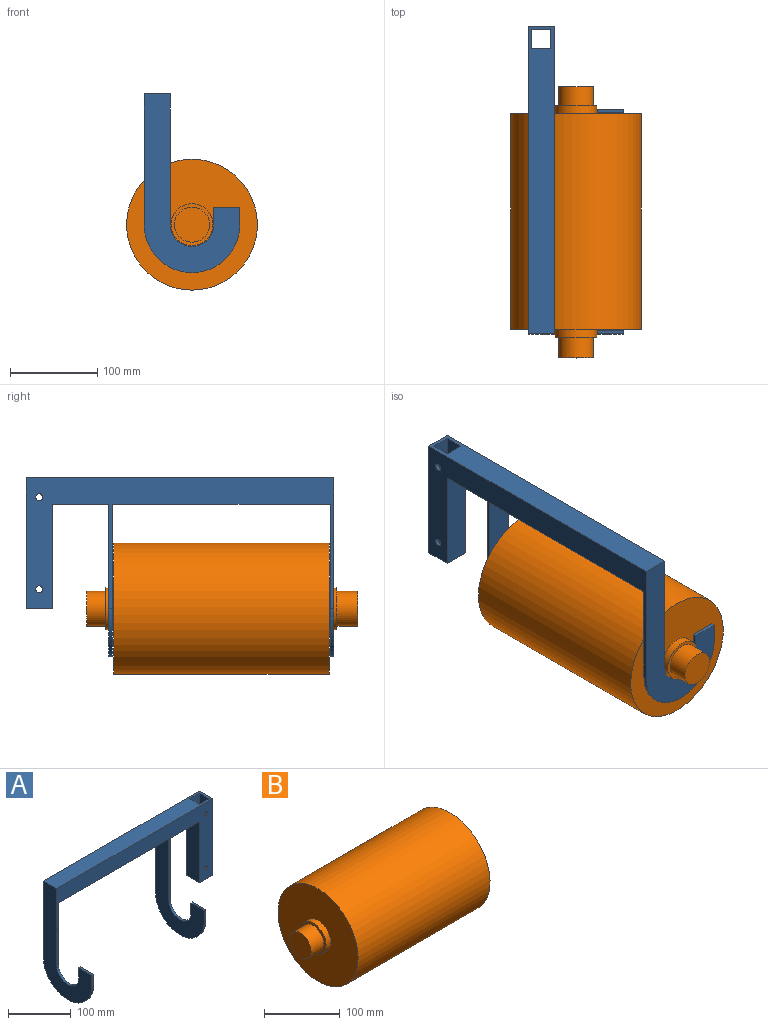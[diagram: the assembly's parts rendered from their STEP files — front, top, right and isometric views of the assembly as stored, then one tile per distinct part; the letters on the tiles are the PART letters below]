
ASSEMBLY  parts=2 mates=1
PART A: 42 faces, bbox 353x110x205 mm
  f0: plane 175x110mm, normal (1,0,0), area 7969.9mm2, adj f1,f7,f13,f14,f15,f16,f17,f27
  f1: plane 353x150mm, normal (0,-1,0), area 15049.5mm2, adj f0,f2,f8,f9,f10,f11,f12,f17
  f2: cylinder r=25mm len=50mm, axis (1,0,0), area 314.2mm2, adj f1,f3,f9,f10
  f3: plane 20x4mm, normal (0,1,0), area 80mm2, adj f2,f4,f9,f10
  f4: plane 30x4mm, normal (0,0,1), area 120mm2, adj f3,f5,f9,f10
  f5: plane 20x4mm, normal (0,-1,0), area 80mm2, adj f4,f6,f9,f10
  f6: cylinder r=55mm len=110mm, axis (1,0,0), area 691.2mm2, adj f5,f7,f9,f10
  f7: plane 353x150mm, normal (0,1,0), area 15049.5mm2, adj f0,f6,f8,f9,f10,f11,f12,f13
  f8: plane 353x30mm, normal (0,0,1), area 10106mm2, adj f1,f7,f9,f22,f24,f25,f28,f29
  f9: plane 205x110mm, normal (-1,0,0), area 8869.9mm2, adj f1,f2,f3,f4,f5,f6,f7,f8
  f10: plane 175x110mm, normal (1,0,0), area 7969.9mm2, adj f1,f2,f3,f4,f5,f6,f7,f11
  f11: plane 250x30mm, normal (0,0,-1), area 7500mm2, adj f1,f7,f10,f12
  f12: plane 175x110mm, normal (-1,0,0), area 7969.9mm2, adj f1,f7,f11,f13,f14,f15,f16,f17
  f13: cylinder r=55mm len=110mm, axis (-1,0,0), area 691.2mm2, adj f0,f7,f12,f14
  f14: plane 20x4mm, normal (0,-1,0), area 80mm2, adj f0,f12,f13,f15
  f15: plane 30x4mm, normal (0,0,1), area 120mm2, adj f0,f12,f14,f16
  f16: plane 20x4mm, normal (0,1,0), area 80mm2, adj f0,f12,f15,f17
  f17: cylinder r=25mm len=50mm, axis (-1,0,0), area 314.2mm2, adj f0,f1,f12,f16
  f18: cylinder r=4mm len=8mm, axis (0,-1,0), area 100.5mm2, adj f7,f29
  f19: cylinder r=4mm len=8mm, axis (0,-1,0), area 100.5mm2, adj f7,f29
  f20: cylinder r=4mm len=8mm, axis (0,-1,0), area 100.5mm2, adj f1,f28
  f21: cylinder r=4mm len=8mm, axis (0,-1,0), area 100.5mm2, adj f1,f28
  f22: plane 150x22mm, normal (1,0,0), area 3300mm2, adj f8,f26,f28,f29
  f23: plane 120x30mm, normal (-1,0,0), area 3600mm2, adj f1,f7,f26,f27
  f24: plane 150x30mm, normal (1,0,0), area 4500mm2, adj f1,f7,f8,f26
  f25: plane 150x22mm, normal (-1,0,0), area 3300mm2, adj f8,f26,f28,f29
  f26: plane 30x30mm, normal (0,0,-1), area 416mm2, adj f1,f7,f22,f23,f24,f25,f28,f29
  f27: plane 65x30mm, normal (0,0,-1), area 1950mm2, adj f0,f1,f7,f23
  f28: plane 150x22mm, normal (0,1,0), area 3199.5mm2, adj f8,f20,f21,f22,f25,f26
  f29: plane 150x22mm, normal (0,-1,0), area 3199.5mm2, adj f8,f18,f19,f22,f25,f26
  f30: plane 22x22mm, normal (1,0,0), area 484mm2, adj f31,f32,f33,f34
  f31: plane 250x22mm, normal (0,-1,0), area 5500mm2, adj f30,f32,f34,f35
  f32: plane 250x22mm, normal (0,0,-1), area 5500mm2, adj f30,f31,f33,f35
  f33: plane 250x22mm, normal (0,1,0), area 5500mm2, adj f30,f32,f34,f35
  f34: plane 250x22mm, normal (0,0,1), area 5500mm2, adj f30,f31,f33,f35
  f35: plane 22x22mm, normal (-1,0,0), area 484mm2, adj f31,f32,f33,f34
  f36: plane 65x22mm, normal (0,0,-1), area 1430mm2, adj f37,f39,f40,f41
  f37: plane 65x22mm, normal (0,-1,0), area 1430mm2, adj f36,f38,f40,f41
  f38: plane 65x22mm, normal (0,0,1), area 1430mm2, adj f37,f39,f40,f41
  f39: plane 65x22mm, normal (0,1,0), area 1430mm2, adj f36,f38,f40,f41
  f40: plane 22x22mm, normal (-1,0,0), area 484mm2, adj f36,f37,f38,f39
  f41: plane 22x22mm, normal (1,0,0), area 484mm2, adj f36,f37,f38,f39
PART B: 11 faces, bbox 311x150x150 mm
  f0: cylinder r=75mm len=247mm, axis (-1,0,0), area 116396mm2, adj f1,f2
  f1: plane 150x150mm, normal (1,0,0), area 15861.9mm2, adj f0,f3
  f2: plane 150x150mm, normal (-1,0,0), area 15861.9mm2, adj f0,f7
  f3: cylinder r=24mm len=48mm, axis (-1,0,0), area 1357.2mm2, adj f1,f4
  f4: plane 48x48mm, normal (1,0,0), area 552.9mm2, adj f3,f5
  f5: cylinder r=20mm len=40mm, axis (-1,0,0), area 2764.6mm2, adj f4,f6
  f6: plane 40x40mm, normal (1,0,0), area 1256.6mm2, adj f5
  f7: cylinder r=24mm len=48mm, axis (1,0,0), area 1357.2mm2, adj f2,f8
  f8: plane 48x48mm, normal (-1,0,0), area 552.9mm2, adj f7,f9
  f9: cylinder r=20mm len=40mm, axis (1,0,0), area 3015.9mm2, adj f8,f10
  f10: plane 40x40mm, normal (-1,0,0), area 1256.6mm2, adj f9
PLACE A rot(axis=(0,0,1),90deg) t=(-376.39,-3.67,993.34)mm
PLACE B rot(axis=(0,0,1),90deg) t=(-376.39,-2.17,993.34)mm
MATE fastened B.f5 <-> A.f2  axis (0,-1,0) through (-376.39,-35.17,993.34)mm
